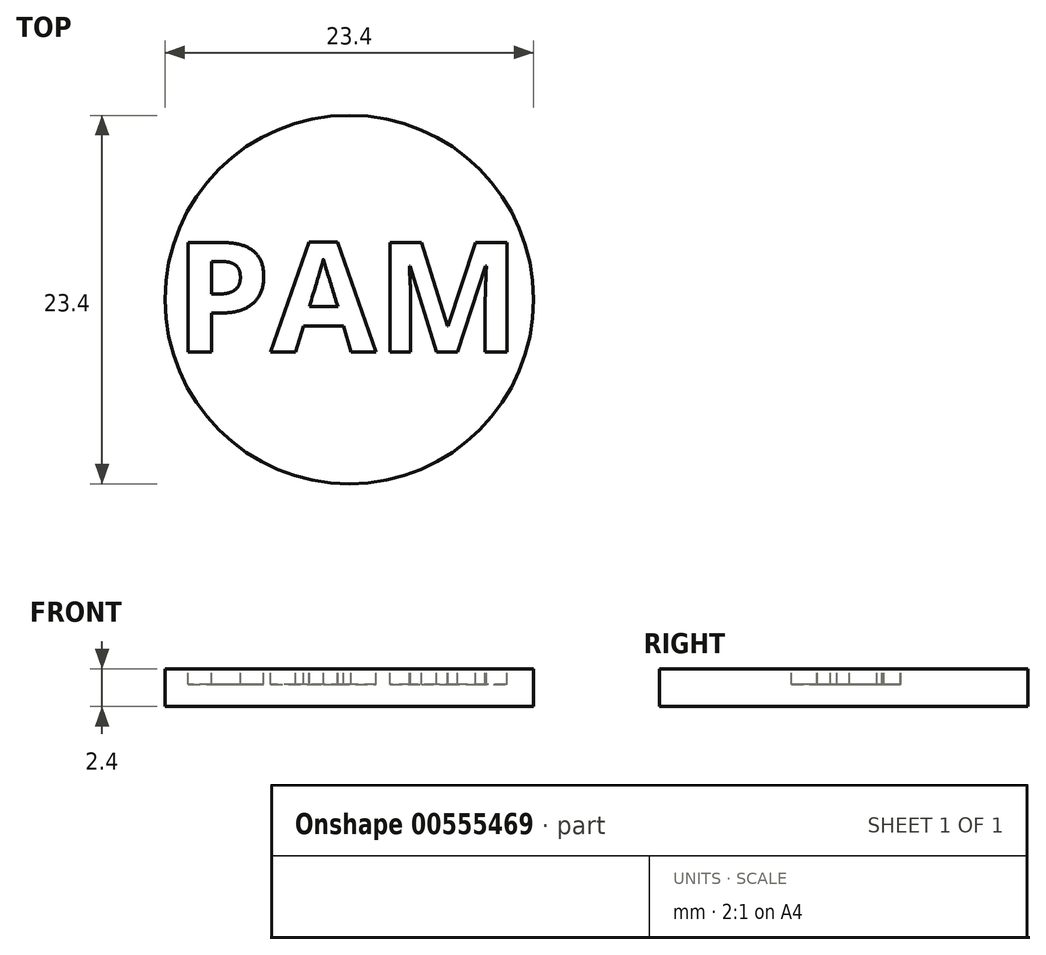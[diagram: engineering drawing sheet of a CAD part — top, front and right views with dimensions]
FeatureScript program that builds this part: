
annotation { "Feature Type Name" : "Feature", "Feature Type Description" : "" }
export const myFeature = defineFeature(function(context is Context, id is Id, definition is map)
    precondition{}
    {
        {
            var Q0;
            Q0=qCreatedBy(makeId("Top.planeOp"),FACE);
            var sketch = newSketch(context, id + "F0", { "sketchPlane" : qUnion([Q0])});
            skCircle(sketch, "E0", {"center": v(0, 0) * mm, "radius": 11.7 * mm});
            skSolve(sketch);
        }
        {
            var Q0;
            Q0=makeQuery(id+"F0.imprint","IMPRINT",FACE,{"disambiguationData":[TD([[makeQuery(id+"F0.imprint","IMPRINT",EDGE,{"derivedFrom":sQuery(id+"F0.wireOp",EDGE,"E0")}),1.0]])]});
            extrude(context, id + "F1", {"entities" : qUnion([Q0]), "depth" : 2.4 * mm, "offsetDistance" : 25 * mm});
        }
        {
            var Q0;
            Q0=makeQuery(id+"F1.opExtrude","CAP_FACE",FACE,{"disambiguationData":[OSD([sQuery(id+"F0.wireOp",EDGE,"E0")])],"isStart":false});
            var sketch = newSketch(context, id + "F2", { "sketchPlane" : qUnion([Q0])});
            skText(sketch, "E1", { "text": "PAM", "fontName": "OpenSans-Bold.ttf"});
            const initialGuessF2  = {"E1": [-0.0111, -0.00332, 1, 0, 0.007]};
            skSetInitialGuess(sketch, initialGuessF2);
            skSolve(sketch);
        }
        {
            var Q0;
            Q0=makeQuery(id+"F2.imprint","IMPRINT",FACE,{"disambiguationData":[TD([[makeQuery(id+"F2.imprint","IMPRINT",EDGE,{"derivedFrom":sQuery(id+"F2.wireOp",EDGE,"E1.sketch_text.stroke-16")}),-1.0]])]});
            var Q1;
            Q1=makeQuery(id+"F2.imprint","IMPRINT",FACE,{"disambiguationData":[TD([[makeQuery(id+"F2.imprint","IMPRINT",EDGE,{"derivedFrom":sQuery(id+"F2.wireOp",EDGE,"E1.sketch_text.stroke-0")}),-1.0]])]});
            var Q2;
            Q2=makeQuery(id+"F2.imprint","IMPRINT",FACE,{"disambiguationData":[TD([[makeQuery(id+"F2.imprint","IMPRINT",EDGE,{"derivedFrom":sQuery(id+"F2.wireOp",EDGE,"E1.sketch_text.stroke-28")}),-1.0]])]});
            extrude(context, id + "F3", {"entities" : qUnion([Q0, Q1, Q2]), "operationType" : NewBodyOperationType.REMOVE, "oppositeDirection" : true, "depth" : 1 * mm, "offsetDistance" : 25 * mm});
        }
    });
